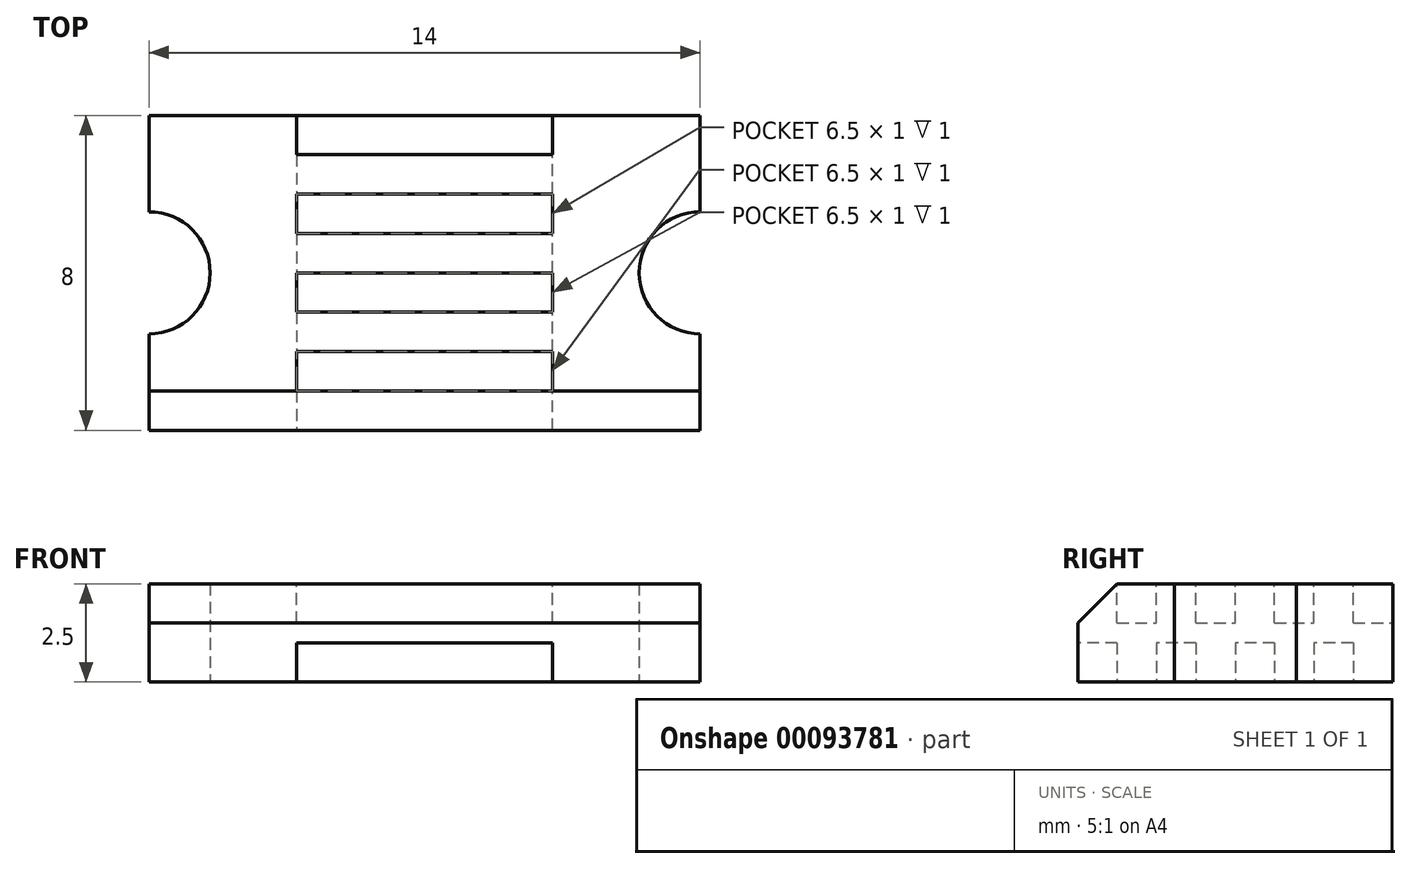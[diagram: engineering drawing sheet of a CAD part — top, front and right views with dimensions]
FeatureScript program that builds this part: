
annotation { "Feature Type Name" : "Feature", "Feature Type Description" : "" }
export const myFeature = defineFeature(function(context is Context, id is Id, definition is map)
    precondition{}
    {
        {
            var Q0;
            Q0=qCreatedBy(makeId("Top.planeOp"),FACE);
            var sketch = newSketch(context, id + "F0", { "sketchPlane" : qUnion([Q0])});
            skLineSegment(sketch, "E0.bottom", {"start": v(-7, 4) * mm, "end": v(7, 4) * mm});
            skLineSegment(sketch, "E0.top", {"start": v(-7, -4) * mm, "end": v(7, -4) * mm});
            skLineSegment(sketch, "E0.left", {"start": v(-11, 0) * mm, "end": v(-11, 0) * mm});
            skLineSegment(sketch, "E0.right", {"start": v(11, 0) * mm, "end": v(11, 0) * mm});
            skPoint(sketch, "E0.middle", {"position": v(0, 0) * mm});
            skPoint(sketch, "E1", {"position": v(-7, 0) * mm});
            skPoint(sketch, "E1.positionSnap0", {"position": v(-11, 0) * mm});
            skLineSegment(sketch, "E2", {"start": v(0, 4) * mm, "end": v(0, -4) * mm, "construction": true});
            skCircle(sketch, "E3", {"center": v(-7, 0) * mm, "radius": 1.55 * mm});
            skCircle(sketch, "E4.MirrorC", {"center": v(7, 0) * mm, "radius": 1.55 * mm});
            skPoint(sketch, "E5.visualSharp", {"position": v(-11, 4) * mm});
            skArc(sketch, "E5.filletArc", {"start": v(-7, 4) * mm, "mid": v(-9.83, 2.83) * mm, "end": v(-11, 0) * mm});
            skPoint(sketch, "E6.visualSharp", {"position": v(-11, -4) * mm});
            skArc(sketch, "E6.filletArc", {"start": v(-11, 0) * mm, "mid": v(-9.83, -2.83) * mm, "end": v(-7, -4) * mm});
            skPoint(sketch, "E7.visualSharp", {"position": v(11, 4) * mm});
            skArc(sketch, "E7.filletArc", {"start": v(11, 0) * mm, "mid": v(9.83, 2.83) * mm, "end": v(7, 4) * mm});
            skPoint(sketch, "E8.visualSharp", {"position": v(11, -4) * mm});
            skArc(sketch, "E8.filletArc", {"start": v(7, -4) * mm, "mid": v(9.83, -2.83) * mm, "end": v(11, 0) * mm});
            skSolve(sketch);
        }
        {
            var Q0;
            Q0=makeQuery(id+"F0.imprint","IMPRINT",FACE,{"disambiguationData":[TD([[makeQuery(id+"F0.imprint","IMPRINT",EDGE,{"derivedFrom":sQuery(id+"F0.wireOp",EDGE,"E0.bottom")}),-1.0]])]});
            extrude(context, id + "F1", {"entities" : qUnion([Q0]), "depth" : 2.5 * mm});
        }
        {
            var Q0;
            Q0=makeQuery(id+"F1.opExtrude","CAP_FACE",FACE,{"disambiguationData":[OSD([sQuery(id+"F0.wireOp",EDGE,"E0.bottom"),sQuery(id+"F0.wireOp",EDGE,"E0.top"),sQuery(id+"F0.wireOp",EDGE,"E3"),sQuery(id+"F0.wireOp",EDGE,"E4.MirrorC"),sQuery(id+"F0.wireOp",EDGE,"E5.filletArc"),sQuery(id+"F0.wireOp",EDGE,"E6.filletArc"),sQuery(id+"F0.wireOp",EDGE,"E7.filletArc"),sQuery(id+"F0.wireOp",EDGE,"E8.filletArc")])],"isStart":false});
            var sketch = newSketch(context, id + "F2", { "sketchPlane" : qUnion([Q0])});
            skLineSegment(sketch, "E9", {"start": v(-7, 4) * mm, "end": v(-7, 1.55) * mm});
            skLineSegment(sketch, "E10", {"start": v(-7, 1.55) * mm, "end": v(-7, -1.55) * mm});
            skLineSegment(sketch, "E11", {"start": v(-7, -1.55) * mm, "end": v(-7, -4) * mm});
            skLineSegment(sketch, "E12", {"start": v(7, 4) * mm, "end": v(7, 1.55) * mm});
            skLineSegment(sketch, "E13", {"start": v(7, 1.55) * mm, "end": v(7, -1.55) * mm});
            skLineSegment(sketch, "E14", {"start": v(7, -1.55) * mm, "end": v(7, -4) * mm});
            skArc(sketch, "E15.0", {"start": v(-7, 4) * mm, "mid": v(-11, 0) * mm, "end": v(-7, -4) * mm});
            skArc(sketch, "E16.0", {"start": v(7, -4) * mm, "mid": v(11, 0) * mm, "end": v(7, 4) * mm});
            skSolve(sketch);
        }
        {
            var Q0;
            {var subQ0=sQuery(id+"F2.wireOp",EDGE,"E9");Q0=makeQuery(id+"F2.imprint","IMPRINT",FACE,{"disambiguationData":[TD([[makeQuery(id+"F2.imprint","IMPRINT",EDGE,{"derivedFrom":subQ0}),-1.0]])]});}
            var Q1;
            {var subQ0=sQuery(id+"F2.wireOp",EDGE,"E12");Q1=makeQuery(id+"F2.imprint","IMPRINT",FACE,{"disambiguationData":[TD([[makeQuery(id+"F2.imprint","IMPRINT",EDGE,{"derivedFrom":subQ0}),1.0]])]});}
            extrude(context, id + "F3", {"entities" : qUnion([Q0, Q1]), "operationType" : NewBodyOperationType.REMOVE, "endBound" : BoundingType.THROUGH_ALL, "oppositeDirection" : true, "depth" : 25 * mm});
        }
        {
            var Q0;
            Q0=makeQuery(id+"F1.opExtrude","CAP_FACE",FACE,{"disambiguationData":[OSD([sQuery(id+"F0.wireOp",EDGE,"E0.bottom"),sQuery(id+"F0.wireOp",EDGE,"E0.top"),sQuery(id+"F0.wireOp",EDGE,"E3"),sQuery(id+"F0.wireOp",EDGE,"E4.MirrorC"),sQuery(id+"F0.wireOp",EDGE,"E5.filletArc"),sQuery(id+"F0.wireOp",EDGE,"E6.filletArc"),sQuery(id+"F0.wireOp",EDGE,"E7.filletArc"),sQuery(id+"F0.wireOp",EDGE,"E8.filletArc")])],"isStart":false});
            var sketch = newSketch(context, id + "F4", { "sketchPlane" : qUnion([Q0])});
            skLineSegment(sketch, "E17.bottom", {"start": v(-3.25, -4) * mm, "end": v(3.25, -4) * mm});
            skLineSegment(sketch, "E17.top", {"start": v(-3.25, 4) * mm, "end": v(3.25, 4) * mm});
            skLineSegment(sketch, "E17.left", {"start": v(-3.25, -4) * mm, "end": v(-3.25, 4) * mm});
            skLineSegment(sketch, "E17.right", {"start": v(3.25, -4) * mm, "end": v(3.25, 4) * mm});
            skPoint(sketch, "E17.middle", {"position": v(0, 0) * mm});
            skLineSegment(sketch, "E18.top", {"start": v(-3.25, -3) * mm, "end": v(3.25, -3) * mm});
            skLineSegment(sketch, "E18.left", {"start": v(-3.25, -4) * mm, "end": v(-3.25, -3) * mm});
            skLineSegment(sketch, "E18.right", {"start": v(3.25, -4) * mm, "end": v(3.25, -3) * mm});
            skLineSegment(sketch, "E19.top", {"start": v(-3.25, 0) * mm, "end": v(3.25, 0) * mm});
            skLineSegment(sketch, "E19.left", {"start": v(-3.25, -3) * mm, "end": v(-3.25, 0) * mm});
            skLineSegment(sketch, "E19.right", {"start": v(3.25, -3) * mm, "end": v(3.25, 0) * mm});
            skLineSegment(sketch, "E20.top", {"start": v(-3.25, 1) * mm, "end": v(3.25, 1) * mm});
            skLineSegment(sketch, "E20.left", {"start": v(-3.25, 0) * mm, "end": v(-3.25, 1) * mm});
            skLineSegment(sketch, "E20.right", {"start": v(3.25, 0) * mm, "end": v(3.25, 1) * mm});
            skLineSegment(sketch, "E21.left", {"start": v(-3.25, 1) * mm, "end": v(-3.25, 4) * mm});
            skLineSegment(sketch, "E21.right", {"start": v(3.25, 1) * mm, "end": v(3.25, 4) * mm});
            skLineSegment(sketch, "E22.bottom", {"start": v(-3.25, -2) * mm, "end": v(3.25, -2) * mm});
            skLineSegment(sketch, "E22.top", {"start": v(-3.25, -1) * mm, "end": v(3.25, -1) * mm});
            skLineSegment(sketch, "E22.left", {"start": v(-3.25, -2) * mm, "end": v(-3.25, -1) * mm});
            skLineSegment(sketch, "E22.right", {"start": v(3.25, -2) * mm, "end": v(3.25, -1) * mm});
            skLineSegment(sketch, "E23.bottom", {"start": v(-3.25, 2) * mm, "end": v(3.25, 2) * mm});
            skLineSegment(sketch, "E23.top", {"start": v(-3.25, 3) * mm, "end": v(3.25, 3) * mm});
            skLineSegment(sketch, "E23.left", {"start": v(-3.25, 2) * mm, "end": v(-3.25, 3) * mm});
            skLineSegment(sketch, "E23.right", {"start": v(3.25, 2) * mm, "end": v(3.25, 3) * mm});
            skSolve(sketch);
        }
        {
            var Q0;
            Q0=makeQuery(id+"F4.imprint","IMPRINT",FACE,{"disambiguationData":[TD([[makeQuery(id+"F4.imprint","IMPRINT",EDGE,{"derivedFrom":sQuery(id+"F4.wireOp",EDGE,"E20.top")}),1.0]])]});
            var Q1;
            Q1=makeQuery(id+"F4.imprint","IMPRINT",FACE,{"disambiguationData":[TD([[makeQuery(id+"F4.imprint","IMPRINT",EDGE,{"derivedFrom":sQuery(id+"F4.wireOp",EDGE,"E18.top")}),1.0]])]});
            var Q2;
            {var subQ0=sQuery(id+"F4.wireOp",EDGE,"E19.top");Q2=makeQuery(id+"F4.imprint","IMPRINT",FACE,{"disambiguationData":[TD([[makeQuery(id+"F4.imprint","IMPRINT",EDGE,{"derivedFrom":subQ0}),-1.0]])]});}
            var Q3;
            {var subQ0=sQuery(id+"F4.wireOp",EDGE,"E17.top");Q3=makeQuery(id+"F4.imprint","IMPRINT",FACE,{"disambiguationData":[TD([[makeQuery(id+"F4.imprint","IMPRINT",EDGE,{"derivedFrom":subQ0}),-1.0]])]});}
            extrude(context, id + "F5", {"entities" : qUnion([Q0, Q1, Q2, Q3]), "operationType" : NewBodyOperationType.REMOVE, "oppositeDirection" : true, "depth" : 1 * mm});
        }
        {
            var Q0;
            Q0=makeQuery(id+"F1.opExtrude","CAP_FACE",FACE,{"disambiguationData":[OSD([sQuery(id+"F0.wireOp",EDGE,"E0.bottom"),sQuery(id+"F0.wireOp",EDGE,"E0.top"),sQuery(id+"F0.wireOp",EDGE,"E3"),sQuery(id+"F0.wireOp",EDGE,"E4.MirrorC"),sQuery(id+"F0.wireOp",EDGE,"E5.filletArc"),sQuery(id+"F0.wireOp",EDGE,"E6.filletArc"),sQuery(id+"F0.wireOp",EDGE,"E7.filletArc"),sQuery(id+"F0.wireOp",EDGE,"E8.filletArc")])],"isStart":true});
            var sketch = newSketch(context, id + "F6", { "sketchPlane" : qUnion([Q0])});
            skLineSegment(sketch, "E24.0.0", {"start": v(-3.25, -1) * mm, "end": v(-3.25, 0) * mm});
            skLineSegment(sketch, "E24.0.1", {"start": v(-3.25, 0) * mm, "end": v(3.25, 0) * mm});
            skLineSegment(sketch, "E24.0.2", {"start": v(3.25, 0) * mm, "end": v(3.25, -1) * mm});
            skLineSegment(sketch, "E24.0.3", {"start": v(3.25, -1) * mm, "end": v(-3.25, -1) * mm});
            skLineSegment(sketch, "E25.0.0", {"start": v(-3.25, 3) * mm, "end": v(-3.25, 4) * mm});
            skLineSegment(sketch, "E25.0.1", {"start": v(-3.25, 4) * mm, "end": v(3.25, 4) * mm});
            skLineSegment(sketch, "E25.0.2", {"start": v(3.25, 4) * mm, "end": v(3.25, 3) * mm});
            skLineSegment(sketch, "E25.0.3", {"start": v(3.25, 3) * mm, "end": v(-3.25, 3) * mm});
            skLineSegment(sketch, "E26.0.0", {"start": v(-3.25, 1) * mm, "end": v(-3.25, 2) * mm});
            skLineSegment(sketch, "E26.0.1", {"start": v(-3.25, 2) * mm, "end": v(3.25, 2) * mm});
            skLineSegment(sketch, "E26.0.2", {"start": v(3.25, 2) * mm, "end": v(3.25, 1) * mm});
            skLineSegment(sketch, "E26.0.3", {"start": v(3.25, 1) * mm, "end": v(-3.25, 1) * mm});
            skLineSegment(sketch, "E27.0.0", {"start": v(-3.25, -3) * mm, "end": v(-3.25, -2) * mm});
            skLineSegment(sketch, "E27.0.1", {"start": v(-3.25, -2) * mm, "end": v(3.25, -2) * mm});
            skLineSegment(sketch, "E27.0.2", {"start": v(3.25, -2) * mm, "end": v(3.25, -3) * mm});
            skLineSegment(sketch, "E27.0.3", {"start": v(3.25, -3) * mm, "end": v(-3.25, -3) * mm});
            skSolve(sketch);
        }
        {
            var Q0;
            Q0=qSketchRegion(id+"F6",true);
            extrude(context, id + "F7", {"entities" : qUnion([Q0]), "operationType" : NewBodyOperationType.REMOVE, "oppositeDirection" : true, "depth" : 1 * mm});
        }
        {
            var Q0;
            Q0=makeQuery(id+"F7.boolean.opBoolean","COPY",EDGE,{"derivedFrom":makeQuery(id+"F7.opExtrude","CAP_EDGE",EDGE,{"disambiguationData":[OSD([sQuery(id+"F6.wireOp",EDGE,"E27.0.3")])],"isStart":true})});
            var Q1;
            Q1=makeQuery(id+"F7.boolean.opBoolean","COPY",EDGE,{"derivedFrom":makeQuery(id+"F7.opExtrude","CAP_EDGE",EDGE,{"disambiguationData":[OSD([sQuery(id+"F6.wireOp",EDGE,"E24.0.3")])],"isStart":true})});
            var Q2;
            Q2=makeQuery(id+"F7.boolean.opBoolean","COPY",EDGE,{"derivedFrom":makeQuery(id+"F7.opExtrude","CAP_EDGE",EDGE,{"disambiguationData":[OSD([sQuery(id+"F6.wireOp",EDGE,"E26.0.3")])],"isStart":true})});
            var Q3;
            Q3=makeQuery(id+"F7.boolean.opBoolean","COPY",EDGE,{"derivedFrom":makeQuery(id+"F7.opExtrude","CAP_EDGE",EDGE,{"disambiguationData":[OSD([sQuery(id+"F6.wireOp",EDGE,"E25.0.3")])],"isStart":true})});
            var Q4;
            Q4=makeQuery(id+"F1.opExtrude","CAP_EDGE",EDGE,{"disambiguationData":[OSD([sQuery(id+"F0.wireOp",EDGE,"E0.top")])],"isStart":false});
            var Q5;
            Q5=makeQuery(id+"F5.boolean.opBoolean","COPY",EDGE,{"derivedFrom":makeQuery(id+"F5.opExtrude","CAP_EDGE",EDGE,{"disambiguationData":[OSD([sQuery(id+"F4.wireOp",EDGE,"E22.bottom")])],"isStart":true})});
            var Q6;
            Q6=makeQuery(id+"F5.boolean.opBoolean","COPY",EDGE,{"derivedFrom":makeQuery(id+"F5.opExtrude","CAP_EDGE",EDGE,{"disambiguationData":[OSD([sQuery(id+"F4.wireOp",EDGE,"E19.top")])],"isStart":true})});
            var Q7;
            Q7=makeQuery(id+"F5.boolean.opBoolean","COPY",EDGE,{"derivedFrom":makeQuery(id+"F5.opExtrude","CAP_EDGE",EDGE,{"disambiguationData":[OSD([sQuery(id+"F4.wireOp",EDGE,"E23.bottom")])],"isStart":true})});
            chamfer(context, id + "F8", {"entities" : qUnion([Q0, Q1, Q2, Q3, Q4, Q5, Q6, Q7]), "width" : 1 * mm, "tangentPropagation" : true});
        }
    });
